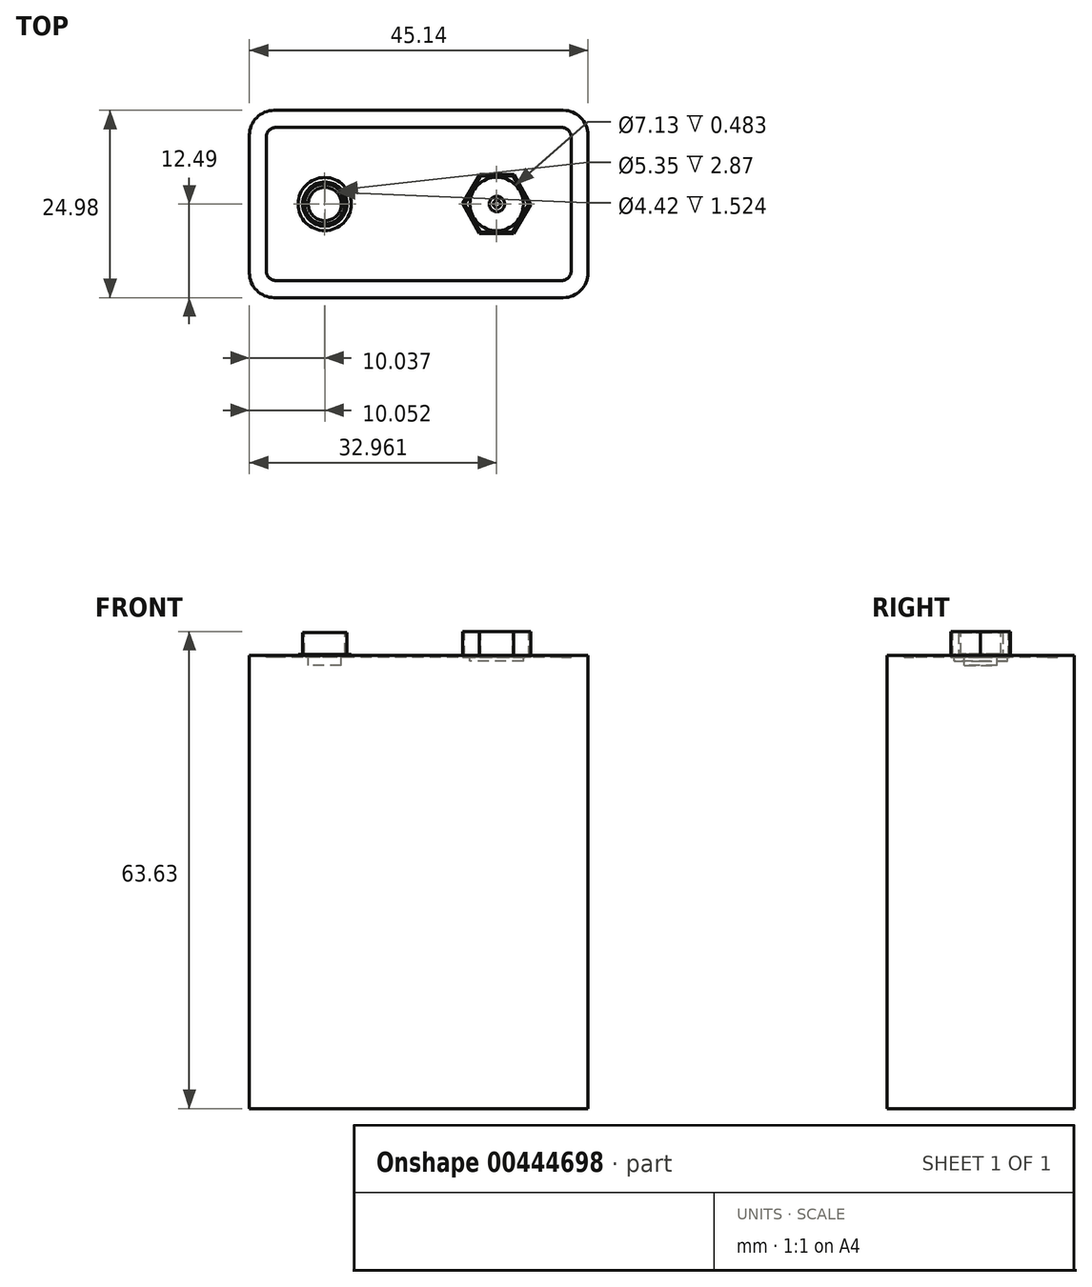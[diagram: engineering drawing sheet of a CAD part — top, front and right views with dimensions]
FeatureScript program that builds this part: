
annotation { "Feature Type Name" : "Feature", "Feature Type Description" : "" }
export const myFeature = defineFeature(function(context is Context, id is Id, definition is map)
    precondition{}
    {
        {
            var Q0;
            Q0=qCreatedBy(makeId("Top.planeOp"),FACE);
            var sketch = newSketch(context, id + "F0", { "sketchPlane" : qUnion([Q0])});
            skLineSegment(sketch, "E0.bottom", {"start": v(22.57, 12.49) * mm, "end": v(-22.57, 12.49) * mm});
            skLineSegment(sketch, "E0.top", {"start": v(22.57, -12.49) * mm, "end": v(-22.57, -12.49) * mm});
            skLineSegment(sketch, "E0.left", {"start": v(22.57, 12.49) * mm, "end": v(22.57, -12.49) * mm});
            skLineSegment(sketch, "E0.right", {"start": v(-22.57, 12.49) * mm, "end": v(-22.57, -12.49) * mm});
            skPoint(sketch, "E0.middle", {"position": v(0, 0) * mm});
            skSolve(sketch);
        }
        {
            var Q0;
            Q0=makeQuery(id+"F0.imprint","IMPRINT",FACE,{"disambiguationData":[TD([[makeQuery(id+"F0.imprint","IMPRINT",EDGE,{"derivedFrom":sQuery(id+"F0.wireOp",EDGE,"E0.bottom")}),1.0]])]});
            extrude(context, id + "F1", {"entities" : qUnion([Q0]), "endBound" : BoundingType.SYMMETRIC, "depth" : 60.45 * mm});
        }
        {
            var Q0;
            Q0=makeQuery(id+"F1.opExtrude","SWEPT_EDGE",EDGE,{"disambiguationData":[OSD([sQuery(id+"F0.wireOp",EDGE,"E0.top"),sQuery(id+"F0.wireOp",EDGE,"E0.right")])]});
            var Q1;
            Q1=makeQuery(id+"F1.opExtrude","SWEPT_EDGE",EDGE,{"disambiguationData":[OSD([sQuery(id+"F0.wireOp",EDGE,"E0.bottom"),sQuery(id+"F0.wireOp",EDGE,"E0.right")])]});
            var Q2;
            Q2=makeQuery(id+"F1.opExtrude","SWEPT_EDGE",EDGE,{"disambiguationData":[OSD([sQuery(id+"F0.wireOp",EDGE,"E0.top"),sQuery(id+"F0.wireOp",EDGE,"E0.left")])]});
            var Q3;
            Q3=makeQuery(id+"F1.opExtrude","SWEPT_EDGE",EDGE,{"disambiguationData":[OSD([sQuery(id+"F0.wireOp",EDGE,"E0.bottom"),sQuery(id+"F0.wireOp",EDGE,"E0.left")])]});
            fillet(context, id + "F2", {"entities" : qUnion([Q0, Q1, Q2, Q3]), "radius" : 3.3 * mm, "tangentPropagation" : true, "allowEdgeOverflow" : false});
        }
        {
            var Q0;
            Q0=makeQuery(id+"F1.opExtrude","CAP_FACE",FACE,{"disambiguationData":[OSD([sQuery(id+"F0.wireOp",EDGE,"E0.bottom"),sQuery(id+"F0.wireOp",EDGE,"E0.top"),sQuery(id+"F0.wireOp",EDGE,"E0.left"),sQuery(id+"F0.wireOp",EDGE,"E0.right")])],"isStart":false});
            var sketch = newSketch(context, id + "F3", { "sketchPlane" : qUnion([Q0])});
            skLineSegment(sketch, "E1.bottom", {"start": v(20.32, 10.21) * mm, "end": v(-20.32, 10.21) * mm});
            skLineSegment(sketch, "E1.top", {"start": v(20.32, -10.21) * mm, "end": v(-20.32, -10.21) * mm});
            skLineSegment(sketch, "E1.left", {"start": v(20.32, 10.21) * mm, "end": v(20.32, -10.21) * mm});
            skLineSegment(sketch, "E1.right", {"start": v(-20.32, 10.21) * mm, "end": v(-20.32, -10.21) * mm});
            skPoint(sketch, "E1.middle", {"position": v(0, 0) * mm});
            skSolve(sketch);
        }
        {
            var Q0;
            Q0=makeQuery(id+"F3.imprint","IMPRINT",FACE,{"disambiguationData":[TD([[makeQuery(id+"F3.imprint","IMPRINT",EDGE,{"derivedFrom":sQuery(id+"F3.wireOp",EDGE,"E1.bottom")}),1.0]])]});
            extrude(context, id + "F4", {"entities" : qUnion([Q0]), "operationType" : NewBodyOperationType.REMOVE, "oppositeDirection" : true, "depth" : 0.25 * mm});
        }
        {
            var Q0;
            Q0=makeQuery(id+"F4.boolean.opBoolean","COPY",EDGE,{"derivedFrom":makeQuery(id+"F4.opExtrude","SWEPT_EDGE",EDGE,{"disambiguationData":[OSD([sQuery(id+"F3.wireOp",EDGE,"E1.bottom"),sQuery(id+"F3.wireOp",EDGE,"E1.right")])]})});
            var Q1;
            Q1=makeQuery(id+"F4.boolean.opBoolean","COPY",EDGE,{"derivedFrom":makeQuery(id+"F4.opExtrude","SWEPT_EDGE",EDGE,{"disambiguationData":[OSD([sQuery(id+"F3.wireOp",EDGE,"E1.top"),sQuery(id+"F3.wireOp",EDGE,"E1.right")])]})});
            var Q2;
            Q2=makeQuery(id+"F4.boolean.opBoolean","COPY",EDGE,{"derivedFrom":makeQuery(id+"F4.opExtrude","SWEPT_EDGE",EDGE,{"disambiguationData":[OSD([sQuery(id+"F3.wireOp",EDGE,"E1.bottom"),sQuery(id+"F3.wireOp",EDGE,"E1.left")])]})});
            var Q3;
            Q3=makeQuery(id+"F4.boolean.opBoolean","COPY",EDGE,{"derivedFrom":makeQuery(id+"F4.opExtrude","SWEPT_EDGE",EDGE,{"disambiguationData":[OSD([sQuery(id+"F3.wireOp",EDGE,"E1.top"),sQuery(id+"F3.wireOp",EDGE,"E1.left")])]})});
            fillet(context, id + "F5", {"entities" : qUnion([Q0, Q1, Q2, Q3]), "radius" : 1.27 * mm, "tangentPropagation" : true, "allowEdgeOverflow" : false});
        }
        {
            var Q0;
            Q0=makeQuery(id+"F4.boolean.opBoolean","COPY",FACE,{"derivedFrom":makeQuery(id+"F4.opExtrude","CAP_FACE",FACE,{"disambiguationData":[OSD([sQuery(id+"F3.wireOp",EDGE,"E1.bottom"),sQuery(id+"F3.wireOp",EDGE,"E1.top"),sQuery(id+"F3.wireOp",EDGE,"E1.left"),sQuery(id+"F3.wireOp",EDGE,"E1.right")])],"isStart":false})});
            var sketch = newSketch(context, id + "F6", { "sketchPlane" : qUnion([Q0])});
            skCircle(sketch, "E2", {"center": v(-12.53, 0) * mm, "radius": 3.54 * mm});
            skCircle(sketch, "E3", {"center": v(-12.53, 0) * mm, "radius": 2.95 * mm});
            skCircle(sketch, "E4.cCircle", {"center": v(10.39, 0) * mm, "radius": 3.94 * mm, "construction": true});
            skLineSegment(sketch, "E4.0", {"start": v(8.15, 3.95) * mm, "end": v(12.7, 3.92) * mm});
            skLineSegment(sketch, "E4.1", {"start": v(12.7, 3.92) * mm, "end": v(14.93, -0.04) * mm});
            skLineSegment(sketch, "E4.2", {"start": v(14.93, -0.04) * mm, "end": v(12.62, -3.95) * mm});
            skLineSegment(sketch, "E4.3", {"start": v(12.62, -3.95) * mm, "end": v(8.08, -3.92) * mm});
            skLineSegment(sketch, "E4.4", {"start": v(8.08, -3.92) * mm, "end": v(5.84, 0.04) * mm});
            skLineSegment(sketch, "E4.5", {"start": v(5.84, 0.04) * mm, "end": v(8.15, 3.95) * mm});
            skPoint(sketch, "E4.0.midPoint", {"position": v(10.42, 3.94) * mm});
            skSolve(sketch);
        }
        {
            var Q0;
            Q0=makeQuery(id+"F6.imprint","IMPRINT",FACE,{"disambiguationData":[TD([[makeQuery(id+"F6.imprint","IMPRINT",EDGE,{"derivedFrom":sQuery(id+"F6.wireOp",EDGE,"E3")}),1.0]])]});
            extrude(context, id + "F7", {"entities" : qUnion([Q0]), "operationType" : NewBodyOperationType.ADD, "depth" : 3.28 * mm});
        }
        {
            var Q0;
            Q0=makeQuery(id+"F6.imprint","IMPRINT",FACE,{"disambiguationData":[TD([[makeQuery(id+"F6.imprint","IMPRINT",EDGE,{"derivedFrom":sQuery(id+"F6.wireOp",EDGE,"E2")}),1.0]])]});
            extrude(context, id + "F8", {"entities" : qUnion([Q0]), "operationType" : NewBodyOperationType.ADD, "depth" : 0.38 * mm});
        }
        {
            var Q0;
            Q0=makeQuery(id+"F6.imprint","IMPRINT",FACE,{"disambiguationData":[TD([[makeQuery(id+"F6.imprint","IMPRINT",EDGE,{"derivedFrom":sQuery(id+"F6.wireOp",EDGE,"E4.0")}),-1.0]])]});
            extrude(context, id + "F9", {"entities" : qUnion([Q0]), "operationType" : NewBodyOperationType.ADD, "depth" : 3.43 * mm});
        }
        {
            var Q0;
            Q0=makeQuery(id+"F9.opExtrude","CAP_FACE",FACE,{"disambiguationData":[OSD([sQuery(id+"F6.wireOp",EDGE,"E4.0"),sQuery(id+"F6.wireOp",EDGE,"E4.1"),sQuery(id+"F6.wireOp",EDGE,"E4.2"),sQuery(id+"F6.wireOp",EDGE,"E4.3"),sQuery(id+"F6.wireOp",EDGE,"E4.4"),sQuery(id+"F6.wireOp",EDGE,"E4.5")])],"isStart":false});
            var sketch = newSketch(context, id + "F10", { "sketchPlane" : qUnion([Q0])});
            skCircle(sketch, "E5.cCircle", {"center": v(10.4, 0) * mm, "radius": 3.72 * mm, "construction": true});
            skLineSegment(sketch, "E5.0", {"start": v(8.28, 3.74) * mm, "end": v(12.57, 3.7) * mm});
            skLineSegment(sketch, "E5.1", {"start": v(12.57, 3.7) * mm, "end": v(14.68, -0.04) * mm});
            skLineSegment(sketch, "E5.2", {"start": v(14.68, -0.04) * mm, "end": v(12.5, -3.74) * mm});
            skLineSegment(sketch, "E5.3", {"start": v(12.5, -3.74) * mm, "end": v(8.21, -3.7) * mm});
            skLineSegment(sketch, "E5.4", {"start": v(8.21, -3.7) * mm, "end": v(6.1, 0.04) * mm});
            skLineSegment(sketch, "E5.5", {"start": v(6.1, 0.04) * mm, "end": v(8.28, 3.74) * mm});
            skPoint(sketch, "E5.0.midPoint", {"position": v(10.42, 3.72) * mm});
            skSolve(sketch);
        }
        {
            var Q0;
            Q0=makeQuery(id+"F10.imprint","IMPRINT",FACE,{"disambiguationData":[TD([[makeQuery(id+"F10.imprint","IMPRINT",EDGE,{"derivedFrom":sQuery(id+"F10.wireOp",EDGE,"E5.0")}),-1.0]])]});
            extrude(context, id + "F11", {"entities" : qUnion([Q0]), "operationType" : NewBodyOperationType.REMOVE, "oppositeDirection" : true, "depth" : 3.45 * mm});
        }
        {
            var Q0;
            Q0=makeQuery(id+"F6.imprint","IMPRINT",FACE,{"disambiguationData":[TD([[makeQuery(id+"F6.imprint","IMPRINT",EDGE,{"derivedFrom":sQuery(id+"F6.wireOp",EDGE,"E4.0")}),-1.0]])]});
            var sketch = newSketch(context, id + "F12", { "sketchPlane" : qUnion([Q0])});
            skCircle(sketch, "E6", {"center": v(10.4, 0) * mm, "radius": 3.57 * mm});
            skSolve(sketch);
        }
        {
            var Q0;
            Q0 = qSketchRegion(id + "F12", true);
            extrude(context, id + "F13", {"entities" : qUnion([Q0]), "operationType" : NewBodyOperationType.REMOVE, "oppositeDirection" : true, "depth" : 0.5 * mm});
        }
        {
            var Q0;
            Q0=makeQuery(id+"F6.imprint","IMPRINT",FACE,{"disambiguationData":[TD([[makeQuery(id+"F6.imprint","IMPRINT",EDGE,{"derivedFrom":sQuery(id+"F6.wireOp",EDGE,"E4.0")}),-1.0]])]});
            var sketch = newSketch(context, id + "F14", { "sketchPlane" : qUnion([Q0])});
            skCircle(sketch, "E7", {"center": v(10.42, 0) * mm, "radius": 1.04 * mm});
            skCircle(sketch, "E8", {"center": v(10.42, 0) * mm, "radius": 0.48 * mm});
            skSolve(sketch);
        }
        {
            var Q0;
            Q0=makeQuery(id+"F14.imprint","IMPRINT",FACE,{"disambiguationData":[TD([[makeQuery(id+"F14.imprint","IMPRINT",EDGE,{"derivedFrom":sQuery(id+"F14.wireOp",EDGE,"E8")}),1.0]])]});
            extrude(context, id + "F15", {"entities" : qUnion([Q0]), "depth" : 0.08 * mm});
        }
        {
            var Q0;
            Q0=makeQuery(id+"F14.imprint","IMPRINT",FACE,{"disambiguationData":[TD([[makeQuery(id+"F14.imprint","IMPRINT",EDGE,{"derivedFrom":sQuery(id+"F14.wireOp",EDGE,"E7")}),1.0]])]});
            extrude(context, id + "F16", {"entities" : qUnion([Q0]), "operationType" : NewBodyOperationType.ADD, "depth" : 0.25 * mm});
        }
        {
            var Q0;
            Q0=makeQuery(id+"F16.opExtrude","CAP_FACE",FACE,{"disambiguationData":[OSD([sQuery(id+"F14.wireOp",EDGE,"E7"),sQuery(id+"F14.wireOp",EDGE,"E8")])],"isStart":false});
            fillet(context, id + "F17", {"entities" : qUnion([Q0]), "radius" : 0.25 * mm, "tangentPropagation" : true, "allowEdgeOverflow" : false});
        }
        {
            var Q0;
            Q0=makeQuery(id+"F7.opExtrude","CAP_FACE",FACE,{"disambiguationData":[OSD([sQuery(id+"F6.wireOp",EDGE,"E3")])],"isStart":false});
            var sketch = newSketch(context, id + "F18", { "sketchPlane" : qUnion([Q0])});
            skCircle(sketch, "E9", {"center": v(-12.53, 0) * mm, "radius": 2.68 * mm});
            skCircle(sketch, "E10", {"center": v(-12.53, 0) * mm, "radius": 0.84 * mm});
            skCircle(sketch, "E11", {"center": v(-12.53, 0) * mm, "radius": 0.48 * mm});
            skSolve(sketch);
        }
        {
            var Q0;
            Q0=makeQuery(id+"F18.imprint","IMPRINT",FACE,{"disambiguationData":[TD([[makeQuery(id+"F18.imprint","IMPRINT",EDGE,{"derivedFrom":sQuery(id+"F18.wireOp",EDGE,"E9")}),1.0]])]});
            extrude(context, id + "F19", {"entities" : qUnion([Q0]), "operationType" : NewBodyOperationType.REMOVE, "oppositeDirection" : true, "depth" : 2.87 * mm});
        }
        {
            var Q0;
            Q0=makeQuery(id+"F18.imprint","IMPRINT",FACE,{"disambiguationData":[TD([[makeQuery(id+"F18.imprint","IMPRINT",EDGE,{"derivedFrom":sQuery(id+"F18.wireOp",EDGE,"E9")}),1.0]])]});
            var sketch = newSketch(context, id + "F20", { "sketchPlane" : qUnion([Q0])});
            skCircle(sketch, "E12", {"center": v(-12.52, 0) * mm, "radius": 2.2 * mm});
            skSolve(sketch);
        }
        {
            var Q0;
            Q0 = qSketchRegion(id + "F20", true);
            extrude(context, id + "F21", {"entities" : qUnion([Q0]), "operationType" : NewBodyOperationType.REMOVE, "oppositeDirection" : true, "depth" : 4.4 * mm});
        }
    });
